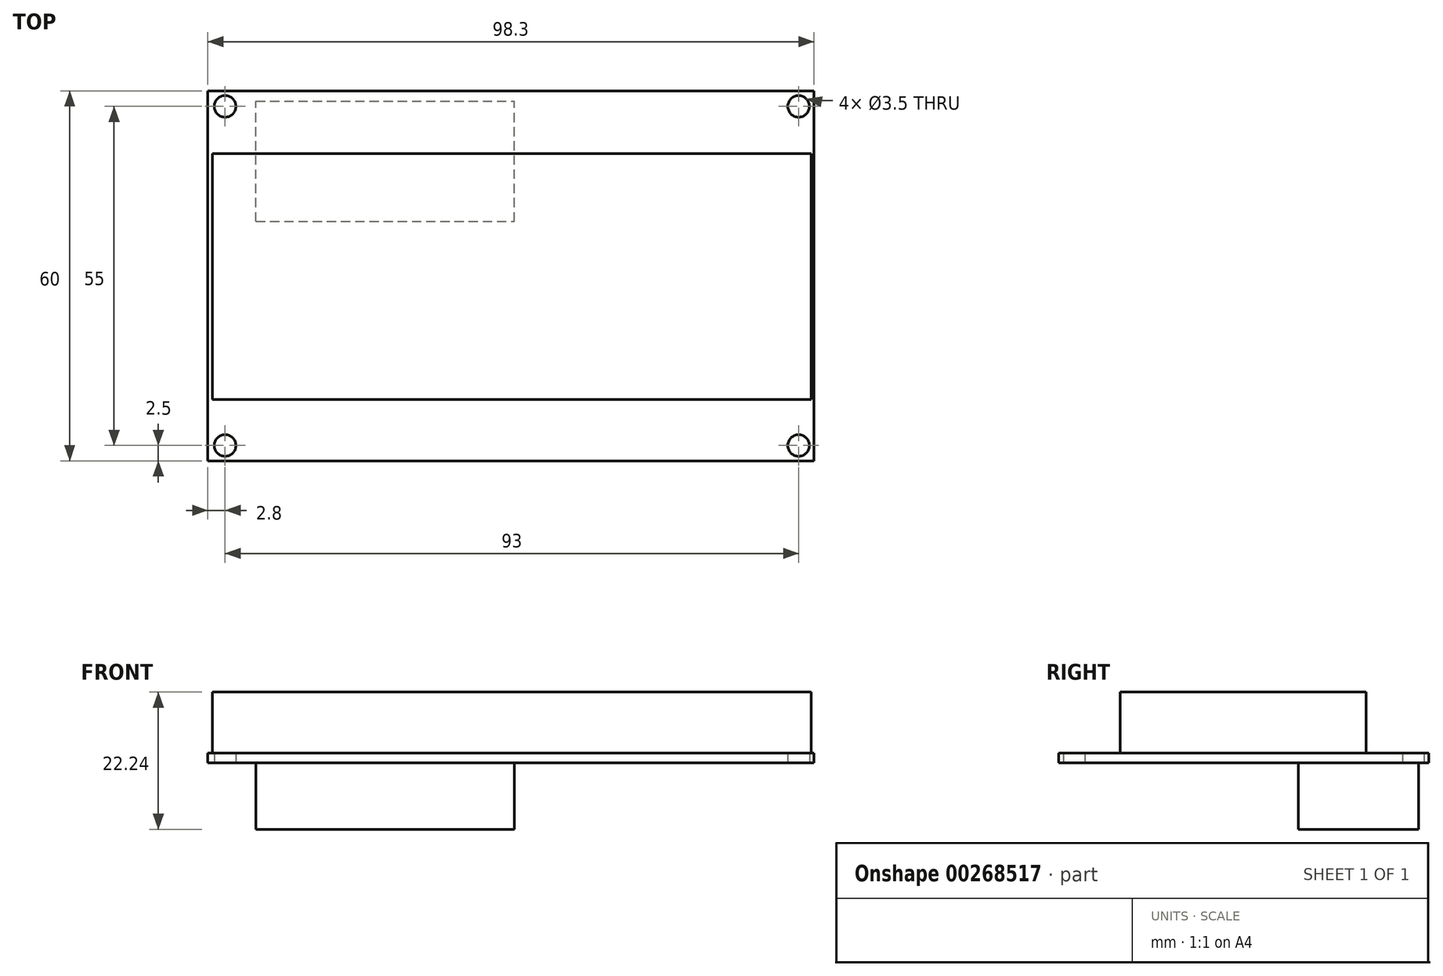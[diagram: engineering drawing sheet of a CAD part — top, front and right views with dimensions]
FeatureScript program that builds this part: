
annotation { "Feature Type Name" : "Feature", "Feature Type Description" : "" }
export const myFeature = defineFeature(function(context is Context, id is Id, definition is map)
    precondition{}
    {
        {
            var Q0;
            Q0=qCreatedBy(makeId("Top.planeOp"),FACE);
            var sketch = newSketch(context, id + "F0", { "sketchPlane" : qUnion([Q0])});
            skLineSegment(sketch, "E0.bottom", {"start": v(49.15, 30) * mm, "end": v(-49.15, 30) * mm});
            skLineSegment(sketch, "E0.top", {"start": v(49.15, -30) * mm, "end": v(-49.15, -30) * mm});
            skLineSegment(sketch, "E0.left", {"start": v(49.15, 30) * mm, "end": v(49.15, -30) * mm});
            skLineSegment(sketch, "E0.right", {"start": v(-49.15, 30) * mm, "end": v(-49.15, -30) * mm});
            skPoint(sketch, "E0.middle", {"position": v(0, 0) * mm});
            skCircle(sketch, "E1", {"center": v(46.65, 27.5) * mm, "radius": 1.75 * mm});
            skCircle(sketch, "E2.MirrorC", {"center": v(46.65, -27.5) * mm, "radius": 1.75 * mm});
            skCircle(sketch, "E3", {"center": v(-46.35, 27.5) * mm, "radius": 1.75 * mm});
            skCircle(sketch, "E4.MirrorC", {"center": v(-46.35, -27.5) * mm, "radius": 1.75 * mm});
            skSolve(sketch);
        }
        {
            var Q0;
            Q0=makeQuery(id+"F0.imprint","IMPRINT",FACE,{"disambiguationData":[TD([[makeQuery(id+"F0.imprint","IMPRINT",EDGE,{"derivedFrom":sQuery(id+"F0.wireOp",EDGE,"E0.bottom")}),1.0]])]});
            var Q1;
            Q1=makeQuery(id+"F0.imprint","IMPRINT",FACE,{"disambiguationData":[TD([[makeQuery(id+"F0.imprint","IMPRINT",EDGE,{"derivedFrom":sQuery(id+"F0.wireOp",EDGE,"rkxBa0un-ti2P-H2wi-MoX2-qtd8EblVNG1E.bottom")}),-1.0]])]});
            extrude(context, id + "F1", {"entities" : qUnion([Q0, Q1]), "depth" : 1.6 * mm});
        }
        {
            var Q0;
            Q0=makeQuery(id+"F1.opExtrude","CAP_FACE",FACE,{"disambiguationData":[OSD([sQuery(id+"F0.wireOp",EDGE,"E0.bottom"),sQuery(id+"F0.wireOp",EDGE,"E0.top"),sQuery(id+"F0.wireOp",EDGE,"E0.left"),sQuery(id+"F0.wireOp",EDGE,"E0.right"),sQuery(id+"F0.wireOp",EDGE,"E1"),sQuery(id+"F0.wireOp",EDGE,"E2.MirrorC"),sQuery(id+"F0.wireOp",EDGE,"E3"),sQuery(id+"F0.wireOp",EDGE,"E4.MirrorC")])],"isStart":false});
            var sketch = newSketch(context, id + "F2", { "sketchPlane" : qUnion([Q0])});
            skLineSegment(sketch, "E5.bottom", {"start": v(-48.4, 19.81) * mm, "end": v(48.7, 19.81) * mm});
            skLineSegment(sketch, "E5.top", {"start": v(-48.4, -20.06) * mm, "end": v(48.7, -20.06) * mm});
            skLineSegment(sketch, "E5.left", {"start": v(-48.4, 19.81) * mm, "end": v(-48.4, -20.06) * mm});
            skLineSegment(sketch, "E5.right", {"start": v(48.7, 19.81) * mm, "end": v(48.7, -20.06) * mm});
            skSolve(sketch);
        }
        {
            var Q0;
            Q0=makeQuery(id+"F2.imprint","IMPRINT",FACE,{"disambiguationData":[TD([[makeQuery(id+"F2.imprint","IMPRINT",EDGE,{"derivedFrom":sQuery(id+"F2.wireOp",EDGE,"E5.bottom")}),-1.0]])]});
            extrude(context, id + "F3", {"entities" : qUnion([Q0]), "depth" : 9.9 * mm});
        }
        {
            var Q0;
            Q0=makeQuery(id+"F0.imprint","IMPRINT",FACE,{"disambiguationData":[TD([[makeQuery(id+"F0.imprint","IMPRINT",EDGE,{"derivedFrom":sQuery(id+"F0.wireOp",EDGE,"E0.bottom")}),1.0]])]});
            var sketch = newSketch(context, id + "F4", { "sketchPlane" : qUnion([Q0])});
            skLineSegment(sketch, "E6.bottom", {"start": v(-41.35, 8.84) * mm, "end": v(0.58, 8.84) * mm});
            skLineSegment(sketch, "E6.top", {"start": v(-41.35, 28.34) * mm, "end": v(0.58, 28.34) * mm});
            skLineSegment(sketch, "E6.left", {"start": v(-41.35, 8.84) * mm, "end": v(-41.35, 28.34) * mm});
            skLineSegment(sketch, "E6.right", {"start": v(0.58, 8.84) * mm, "end": v(0.58, 28.34) * mm});
            skSolve(sketch);
        }
        {
            var Q0;
            Q0=makeQuery(id+"F4.imprint","IMPRINT",FACE,{"disambiguationData":[TD([[makeQuery(id+"F4.imprint","IMPRINT",EDGE,{"derivedFrom":sQuery(id+"F4.wireOp",EDGE,"E6.bottom")}),1.0]])]});
            extrude(context, id + "F5", {"entities" : qUnion([Q0]), "oppositeDirection" : true, "depth" : 10.75 * mm});
        }
    });
